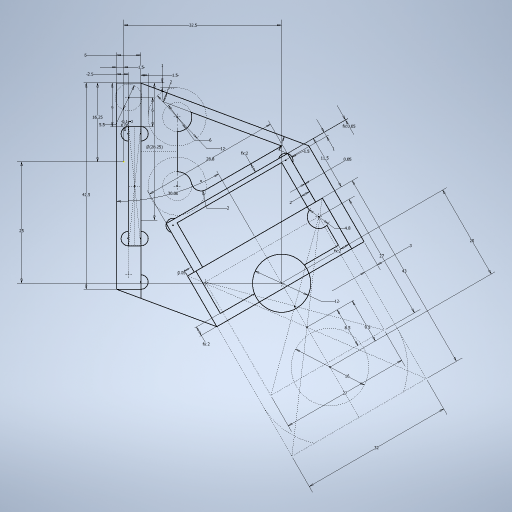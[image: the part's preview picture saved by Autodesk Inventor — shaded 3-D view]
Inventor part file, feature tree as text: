
AUTODESK INVENTOR PART (.ipt)
format: ipt  version: 2024.2 (Build 282272000, 272)  size: 334,848 bytes
history: native  units: mm
features: sketch x1
ambient origin geometry x8: Origin, YZ Plane, XZ Plane, XY Plane, X Axis, Y Axis, Z Axis, Center Point
feature tree (1):
  sketch  "Sketch1"  dims[d1=16.25mm d2=1.5mm d3=42.5mm d4=5.0mm d5=32.0mm d6=43.0mm d7=27.0mm d8=27.0mm d9=16.0mm d11=9.5mm d12=8.5mm d14=30.0deg d15=25.0mm d16=32.5mm d18=20.0mm d19=28.8mm d20=11.5mm d23=0.05mm d24=0.05mm d25=1.5mm d26=3.0mm d28=9.0mm d29=2.5mm d30=0.05mm d31=0.1mm d32=6.0mm d34=0.05mm d35=12.0mm d36=6.0mm d39=5.5mm d44=1.5mm d45=1.0mm d46=28.25mm d47=12.0mm d48=3.0mm d50=2.0mm d51=2.0mm d52=2.0mm d53=4.8mm d54=2.0mm d55=2.0mm d57=1.0mm d58=2.0mm]
